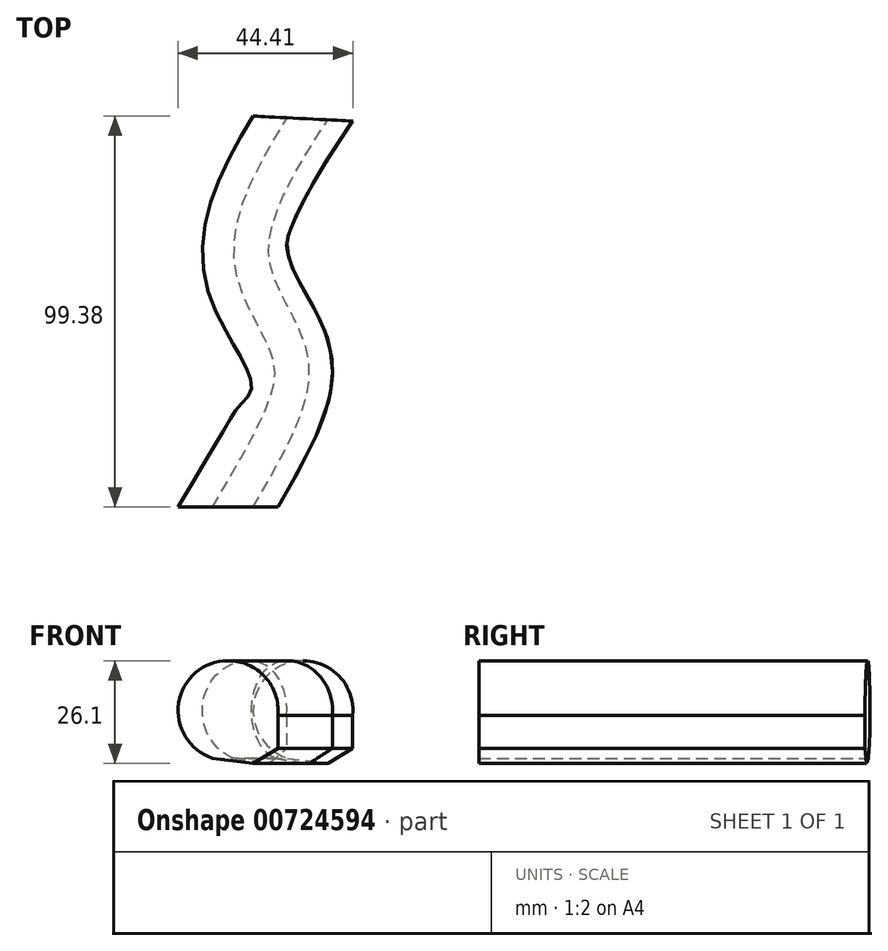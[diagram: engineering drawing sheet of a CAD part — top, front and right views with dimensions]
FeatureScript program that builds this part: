
annotation { "Feature Type Name" : "Feature", "Feature Type Description" : "" }
export const myFeature = defineFeature(function(context is Context, id is Id, definition is map)
    precondition{}
    {
        {
            var Q0;
            Q0=qCreatedBy(makeId("Front.planeOp"),FACE);
            var sketch = newSketch(context, id + "F0", { "sketchPlane" : qUnion([Q0])});
            skLineSegment(sketch, "E0", {"start": v(38.97, 12.42) * mm, "end": v(49.26, 11.08) * mm});
            skLineSegment(sketch, "E1", {"start": v(49.26, 11.08) * mm, "end": v(55.59, 14.91) * mm});
            skLineSegment(sketch, "E2", {"start": v(55.59, 14.91) * mm, "end": v(55.59, 23.34) * mm});
            skArc(sketch, "E3", {"start": v(55.59, 23.34) * mm, "mid": v(35.96, 35.1) * mm, "end": v(38.97, 12.42) * mm});
            skSolve(sketch);
        }
        {
            var Q0;
            Q0=qCreatedBy(makeId("Top.planeOp"),FACE);
            var sketch = newSketch(context, id + "F1", { "sketchPlane" : qUnion([Q0])});
            skFitSpline(sketch, "E4", {"points": [v(44.25, 0) * mm, v(58.63, 38.6) * mm, v(49.5, 60.9) * mm, v(63.28, 98.68) * mm], "startDerivative": vector(95.95, 164.33) * mm, "endDerivative": vector(86.7, 132.82) * mm});
            skSolve(sketch);
        }
        {
            var Q0;
            Q0=makeQuery(id+"F0.imprint","IMPRINT",FACE,{"disambiguationData":[TD([[makeQuery(id+"F0.imprint","IMPRINT",EDGE,{"derivedFrom":sQuery(id+"F0.wireOp",EDGE,"E0")}),1.0]])]});
            var Q1;
            Q1=sQuery(id+"F1.wireOp",EDGE,"E4");
            sweep(context, id + "F2", {"profiles" : qUnion([Q0]), "path" : qUnion([Q1])});
        }
    });
